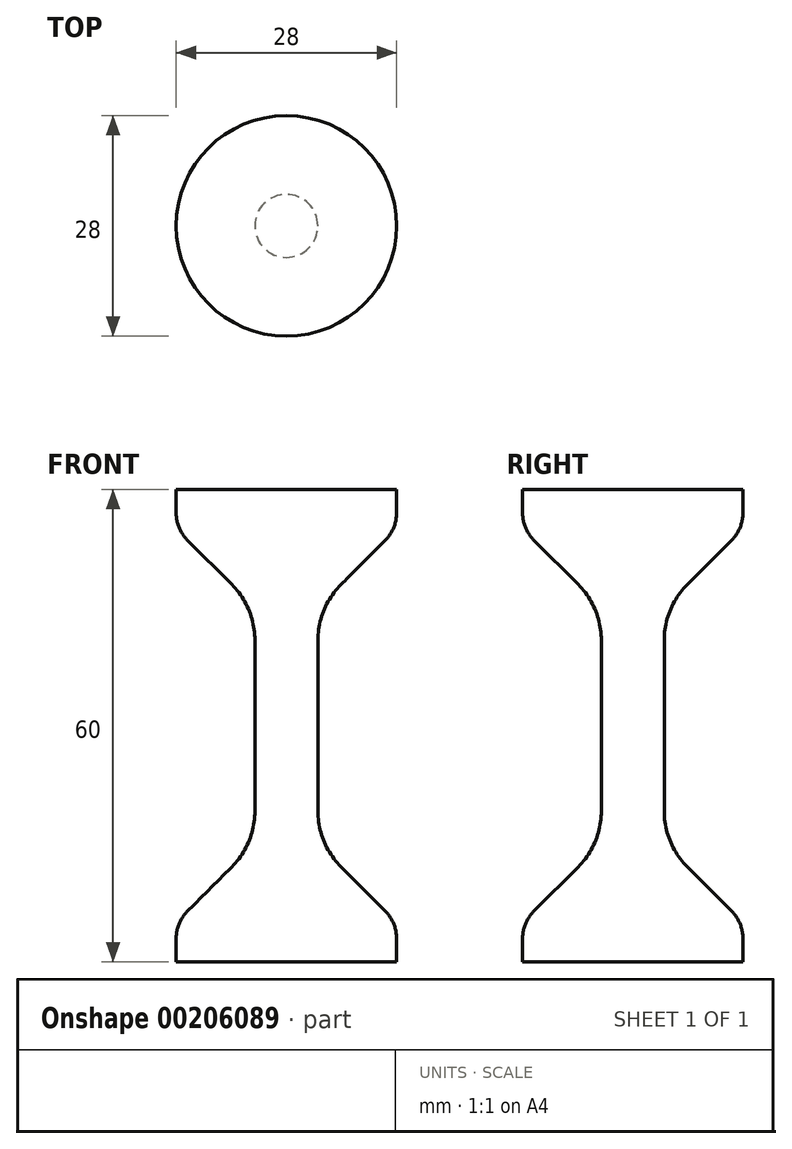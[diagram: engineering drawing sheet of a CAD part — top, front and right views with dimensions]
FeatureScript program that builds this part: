
annotation { "Feature Type Name" : "Feature", "Feature Type Description" : "" }
export const myFeature = defineFeature(function(context is Context, id is Id, definition is map)
    precondition{}
    {
        {
            var Q0;
            Q0=qCreatedBy(makeId("Front.planeOp"),FACE);
            var sketch = newSketch(context, id + "F0", { "sketchPlane" : qUnion([Q0])});
            skLineSegment(sketch, "E0", {"start": v(0, 30) * mm, "end": v(0, -30) * mm});
            skLineSegment(sketch, "E1", {"start": v(0, -30) * mm, "end": v(14, -30) * mm});
            skLineSegment(sketch, "E2", {"start": v(14, -30) * mm, "end": v(14, -25) * mm});
            skLineSegment(sketch, "E3", {"start": v(14, -25) * mm, "end": v(4, -15) * mm});
            skLineSegment(sketch, "E4", {"start": v(4, -15) * mm, "end": v(4, 0) * mm});
            skLineSegment(sketch, "E5", {"start": v(4, 0) * mm, "end": v(4, 15) * mm});
            skLineSegment(sketch, "E6", {"start": v(4, 15) * mm, "end": v(14, 25) * mm});
            skLineSegment(sketch, "E7", {"start": v(14, 25) * mm, "end": v(14, 30) * mm});
            skLineSegment(sketch, "E8", {"start": v(14, 30) * mm, "end": v(0, 30) * mm});
            skSolve(sketch);
        }
        {
            var Q0;
            Q0 = qSketchRegion(id + "F0", true);
            var Q1;
            Q1=sQuery(id+"F0.wireOp",EDGE,"E0");
            revolve(context, id + "F1", {"entities" : qUnion([Q0]), "axis" : qUnion([Q1]), "revolveType" : RevolveType.FULL});
        }
        {
            var Q0;
            Q0=makeQuery(id+"F1.opRevolve","SWEPT_EDGE",EDGE,{"disambiguationData":[OSD([sQuery(id+"F0.wireOp",EDGE,"E5"),sQuery(id+"F0.wireOp",EDGE,"E6")])]});
            var Q1;
            Q1=makeQuery(id+"F1.opRevolve","SWEPT_EDGE",EDGE,{"disambiguationData":[OSD([sQuery(id+"F0.wireOp",EDGE,"E3"),sQuery(id+"F0.wireOp",EDGE,"E4")])]});
            fillet(context, id + "F2", {"entities" : qUnion([Q0, Q1]), "radius" : 10 * mm, "tangentPropagation" : true, "allowEdgeOverflow" : false});
        }
        {
            var Q0;
            Q0=makeQuery(id+"F1.opRevolve","SWEPT_EDGE",EDGE,{"disambiguationData":[OSD([sQuery(id+"F0.wireOp",EDGE,"E6"),sQuery(id+"F0.wireOp",EDGE,"E7")])]});
            var Q1;
            Q1=makeQuery(id+"F1.opRevolve","SWEPT_EDGE",EDGE,{"disambiguationData":[OSD([sQuery(id+"F0.wireOp",EDGE,"E2"),sQuery(id+"F0.wireOp",EDGE,"E3")])]});
            fillet(context, id + "F3", {"entities" : qUnion([Q0, Q1]), "radius" : 5 * mm, "tangentPropagation" : true, "allowEdgeOverflow" : false});
        }
    });
